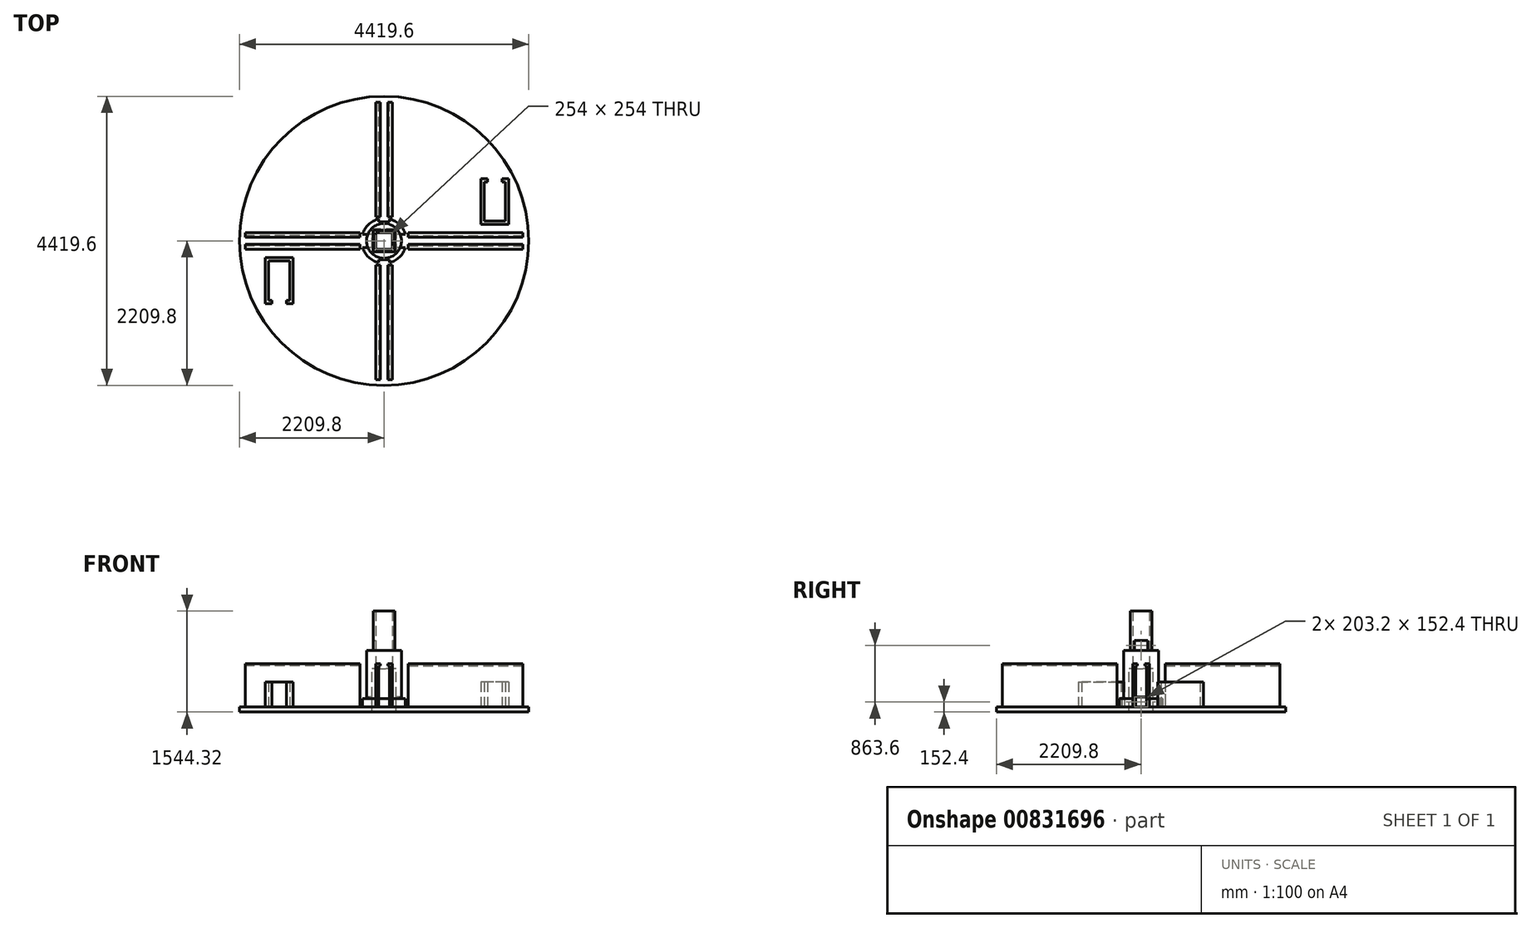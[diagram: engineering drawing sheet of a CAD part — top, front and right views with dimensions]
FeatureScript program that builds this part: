
annotation { "Feature Type Name" : "Feature", "Feature Type Description" : "" }
export const myFeature = defineFeature(function(context is Context, id is Id, definition is map)
    precondition{}
    {
        {
            var Q0;
            Q0=qCreatedBy(makeId("Top.planeOp"),FACE);
            var sketch = newSketch(context, id + "F0", { "sketchPlane" : qUnion([Q0])});
            skCircle(sketch, "E0", {"center": v(0, 0) * mm, "radius": 2209.8 * mm});
            skCircle(sketch, "E1", {"center": v(0, 0) * mm, "radius": 266.7 * mm});
            skLineSegment(sketch, "E2.bottom", {"start": v(-127, -127) * mm, "end": v(127, -127) * mm});
            skLineSegment(sketch, "E2.top", {"start": v(-127, 127) * mm, "end": v(127, 127) * mm});
            skLineSegment(sketch, "E2.left", {"start": v(-127, -127) * mm, "end": v(-127, 127) * mm});
            skLineSegment(sketch, "E2.right", {"start": v(127, -127) * mm, "end": v(127, 127) * mm});
            skLineSegment(sketch, "E3.bottom", {"start": v(-177.8, 177.8) * mm, "end": v(177.8, 177.8) * mm});
            skLineSegment(sketch, "E3.top", {"start": v(-177.8, -177.8) * mm, "end": v(177.8, -177.8) * mm});
            skLineSegment(sketch, "E3.left", {"start": v(-177.8, 177.8) * mm, "end": v(-177.8, -177.8) * mm});
            skLineSegment(sketch, "E3.right", {"start": v(177.8, 177.8) * mm, "end": v(177.8, -177.8) * mm});
            skLineSegment(sketch, "E4.bottom", {"start": v(182.88, 182.88) * mm, "end": v(-182.88, 182.88) * mm});
            skLineSegment(sketch, "E4.top", {"start": v(182.88, -182.88) * mm, "end": v(-182.88, -182.88) * mm});
            skLineSegment(sketch, "E4.left", {"start": v(182.88, 182.88) * mm, "end": v(182.88, -182.88) * mm});
            skLineSegment(sketch, "E4.right", {"start": v(-182.88, 182.88) * mm, "end": v(-182.88, -182.88) * mm});
            skPoint(sketch, "E5", {"position": v(0, 266.7) * mm});
            skPoint(sketch, "E6", {"position": v(266.7, 0) * mm});
            skPoint(sketch, "E7", {"position": v(0, -266.7) * mm});
            skLineSegment(sketch, "E8.bottom", {"start": v(-127, -2120.9) * mm, "end": v(127, -2120.9) * mm});
            skLineSegment(sketch, "E8.top", {"start": v(-127, -368.3) * mm, "end": v(127, -368.3) * mm});
            skLineSegment(sketch, "E8.left", {"start": v(-127, -2120.9) * mm, "end": v(-127, -368.3) * mm});
            skLineSegment(sketch, "E8.right", {"start": v(127, -2120.9) * mm, "end": v(127, -368.3) * mm});
            skLineSegment(sketch, "E9.bottom", {"start": v(368.3, -127) * mm, "end": v(2120.9, -127) * mm});
            skLineSegment(sketch, "E9.top", {"start": v(368.3, 127) * mm, "end": v(2120.9, 127) * mm});
            skLineSegment(sketch, "E9.left", {"start": v(368.3, -127) * mm, "end": v(368.3, 127) * mm});
            skLineSegment(sketch, "E9.right", {"start": v(2120.9, -127) * mm, "end": v(2120.9, 127) * mm});
            skLineSegment(sketch, "E10.bottom", {"start": v(-127, 368.3) * mm, "end": v(127, 368.3) * mm});
            skLineSegment(sketch, "E10.top", {"start": v(-127, 2120.9) * mm, "end": v(127, 2120.9) * mm});
            skLineSegment(sketch, "E10.left", {"start": v(-127, 368.3) * mm, "end": v(-127, 2120.9) * mm});
            skLineSegment(sketch, "E10.right", {"start": v(127, 368.3) * mm, "end": v(127, 2120.9) * mm});
            skCircle(sketch, "E11", {"center": v(0, 0) * mm, "radius": 368.3 * mm});
            skPoint(sketch, "E12", {"position": v(0, 368.3) * mm});
            skPoint(sketch, "E13", {"position": v(368.3, 0) * mm});
            skPoint(sketch, "E14", {"position": v(0, -368.3) * mm});
            skPoint(sketch, "E15", {"position": v(-266.7, 0) * mm});
            skPoint(sketch, "E15.positionSnap0", {"position": v(-177.8, 0) * mm});
            skPoint(sketch, "E16", {"position": v(-368.3, 0) * mm});
            skLineSegment(sketch, "E17.bottom", {"start": v(-2120.9, -127) * mm, "end": v(-368.3, -127) * mm});
            skLineSegment(sketch, "E17.top", {"start": v(-2120.9, 127) * mm, "end": v(-368.3, 127) * mm});
            skLineSegment(sketch, "E17.left", {"start": v(-2120.9, -127) * mm, "end": v(-2120.9, 127) * mm});
            skLineSegment(sketch, "E17.right", {"start": v(-368.3, -127) * mm, "end": v(-368.3, 127) * mm});
            skCircle(sketch, "E18", {"center": v(0, 0) * mm, "radius": 342.9 * mm});
            skLineSegment(sketch, "E19.bottom", {"start": v(1854.2, 304.8) * mm, "end": v(1529.08, 304.8) * mm});
            skLineSegment(sketch, "E19.top", {"start": v(1854.2, 901.7) * mm, "end": v(1529.08, 901.7) * mm});
            skLineSegment(sketch, "E19.left", {"start": v(1854.2, 304.8) * mm, "end": v(1854.2, 901.7) * mm});
            skLineSegment(sketch, "E19.right", {"start": v(1529.08, 304.8) * mm, "end": v(1529.08, 901.7) * mm});
            skLineSegment(sketch, "E20.bottom", {"start": v(1905, 254) * mm, "end": v(1478.28, 254) * mm});
            skLineSegment(sketch, "E20.top", {"start": v(1905, 952.5) * mm, "end": v(1478.28, 952.5) * mm});
            skLineSegment(sketch, "E20.left", {"start": v(1905, 254) * mm, "end": v(1905, 952.5) * mm});
            skLineSegment(sketch, "E20.right", {"start": v(1478.28, 254) * mm, "end": v(1478.28, 952.5) * mm});
            skLineSegment(sketch, "E21", {"start": v(1579.88, 901.7) * mm, "end": v(1579.88, 952.5) * mm});
            skLineSegment(sketch, "E22", {"start": v(1803.4, 901.7) * mm, "end": v(1803.4, 952.5) * mm});
            skLineSegment(sketch, "E23.bottom", {"start": v(-1765.3, -304.8) * mm, "end": v(-1440.18, -304.8) * mm});
            skLineSegment(sketch, "E23.top", {"start": v(-1765.3, -909.32) * mm, "end": v(-1440.18, -909.32) * mm});
            skLineSegment(sketch, "E23.left", {"start": v(-1765.3, -304.8) * mm, "end": v(-1765.3, -909.32) * mm});
            skLineSegment(sketch, "E23.right", {"start": v(-1440.18, -304.8) * mm, "end": v(-1440.18, -909.32) * mm});
            skPoint(sketch, "E23.middle", {"position": v(-1602.74, -607.06) * mm});
            skLineSegment(sketch, "E24.bottom", {"start": v(-1389.38, -960.12) * mm, "end": v(-1816.1, -960.12) * mm});
            skLineSegment(sketch, "E24.top", {"start": v(-1389.38, -254) * mm, "end": v(-1816.1, -254) * mm});
            skLineSegment(sketch, "E24.left", {"start": v(-1389.38, -960.12) * mm, "end": v(-1389.38, -254) * mm});
            skLineSegment(sketch, "E24.right", {"start": v(-1816.1, -960.12) * mm, "end": v(-1816.1, -254) * mm});
            skLineSegment(sketch, "E25", {"start": v(-1490.98, -909.32) * mm, "end": v(-1490.98, -960.12) * mm});
            skLineSegment(sketch, "E26", {"start": v(-1714.5, -960.12) * mm, "end": v(-1714.5, -909.32) * mm});
            skSolve(sketch);
        }
        {
            var Q0;
            Q0=makeQuery(id+"F0.imprint","IMPRINT",FACE,{"disambiguationData":[TD([[makeQuery(id+"F0.imprint","IMPRINT",EDGE,{"derivedFrom":sQuery(id+"F0.wireOp",EDGE,"E10.top")}),-1.0]])]});
            var Q1;
            Q1=makeQuery(id+"F0.imprint","IMPRINT",FACE,{"disambiguationData":[TD([[makeQuery(id+"F0.imprint","IMPRINT",EDGE,{"derivedFrom":sQuery(id+"F0.wireOp",EDGE,"E1")}),-1.0]])]});
            var Q2;
            Q2=makeQuery(id+"F0.imprint","IMPRINT",FACE,{"disambiguationData":[TD([[makeQuery(id+"F0.imprint","IMPRINT",EDGE,{"derivedFrom":sQuery(id+"F0.wireOp",EDGE,"E1")}),1.0]])]});
            var Q3;
            {var subQ4=sQuery(id+"F0.wireOp",EDGE,"E9.bottom");Q3=makeQuery(id+"F0.imprint","IMPRINT",FACE,{"disambiguationData":[TD([[makeQuery(id+"F0.imprint","IMPRINT",EDGE,{"derivedFrom":subQ4}),1.0]])]});}
            var Q4;
            {var subQ0=sQuery(id+"F0.wireOp",EDGE,"E17.bottom");Q4=makeQuery(id+"F0.imprint","IMPRINT",FACE,{"disambiguationData":[TD([[makeQuery(id+"F0.imprint","IMPRINT",EDGE,{"derivedFrom":subQ0}),1.0]])]});}
            var Q5;
            Q5=makeQuery(id+"F0.imprint","IMPRINT",FACE,{"disambiguationData":[TD([[makeQuery(id+"F0.imprint","IMPRINT",EDGE,{"derivedFrom":sQuery(id+"F0.wireOp",EDGE,"E8.bottom")}),1.0]])]});
            var Q6;
            Q6=makeQuery(id+"F0.imprint","IMPRINT",FACE,{"disambiguationData":[TD([[makeQuery(id+"F0.imprint","IMPRINT",EDGE,{"derivedFrom":sQuery(id+"F0.wireOp",EDGE,"E18")}),-1.0]])]});
            var Q7;
            Q7=makeQuery(id+"F0.imprint","IMPRINT",FACE,{"disambiguationData":[TD([[makeQuery(id+"F0.imprint","IMPRINT",EDGE,{"derivedFrom":sQuery(id+"F0.wireOp",EDGE,"E0")}),1.0]])]});
            var Q8;
            Q8=makeQuery(id+"F0.imprint","IMPRINT",FACE,{"disambiguationData":[TD([[makeQuery(id+"F0.imprint","IMPRINT",EDGE,{"derivedFrom":sQuery(id+"F0.wireOp",EDGE,"b8a19175-b3a9-4f45-8a98-ed4f9f6c6702.bottom")}),-1.0]])]});
            var Q9;
            Q9=makeQuery(id+"F0.imprint","IMPRINT",FACE,{"disambiguationData":[TD([[makeQuery(id+"F0.imprint","IMPRINT",EDGE,{"derivedFrom":sQuery(id+"F0.wireOp",EDGE,"7914a9b4-7248-453b-a2e4-3dba9f99fffc.bottom")}),1.0]])]});
            var Q10;
            {var subQ0=sQuery(id+"F0.wireOp",EDGE,"TmSJG6FK-Om5E-kqqE-cBKC-40XiXbPmcmxI");Q10=makeQuery(id+"F0.imprint","IMPRINT",FACE,{"disambiguationData":[TD([[makeQuery(id+"F0.imprint","IMPRINT",EDGE,{"derivedFrom":subQ0}),1.0]])]});}
            var Q11;
            Q11=makeQuery(id+"F0.imprint","IMPRINT",FACE,{"disambiguationData":[TD([[makeQuery(id+"F0.imprint","IMPRINT",EDGE,{"derivedFrom":sQuery(id+"F0.wireOp",EDGE,"wxg1OY8f-ebEG-U6Dd-82FZ-Xdf4qu9MraA2.bottom")}),1.0]])]});
            var Q12;
            {var subQ0=sQuery(id+"F0.wireOp",EDGE,"mW7lPLey-tL3F-X1Fa-1OeG-OaxEq5PTPofp");Q12=makeQuery(id+"F0.imprint","IMPRINT",FACE,{"disambiguationData":[TD([[makeQuery(id+"F0.imprint","IMPRINT",EDGE,{"derivedFrom":subQ0}),-1.0]])]});}
            var Q13;
            Q13=makeQuery(id+"F0.imprint","IMPRINT",FACE,{"disambiguationData":[TD([[makeQuery(id+"F0.imprint","IMPRINT",EDGE,{"derivedFrom":sQuery(id+"F0.wireOp",EDGE,"IBWuTJHf-9YuP-0ksT-Em6A-mQtnpUZ14kUv.top")}),1.0]])]});
            var Q14;
            Q14=makeQuery(id+"F0.imprint","IMPRINT",FACE,{"disambiguationData":[TD([[makeQuery(id+"F0.imprint","IMPRINT",EDGE,{"derivedFrom":sQuery(id+"F0.wireOp",EDGE,"E19.bottom")}),-1.0]])]});
            var Q15;
            Q15=makeQuery(id+"F0.imprint","IMPRINT",FACE,{"disambiguationData":[TD([[makeQuery(id+"F0.imprint","IMPRINT",EDGE,{"derivedFrom":sQuery(id+"F0.wireOp",EDGE,"E19.bottom")}),1.0]])]});
            var Q16;
            {var subQ0=sQuery(id+"F0.wireOp",EDGE,"E21");Q16=makeQuery(id+"F0.imprint","IMPRINT",FACE,{"disambiguationData":[TD([[makeQuery(id+"F0.imprint","IMPRINT",EDGE,{"derivedFrom":subQ0}),-1.0]])]});}
            var Q17;
            Q17=makeQuery(id+"F0.imprint","IMPRINT",FACE,{"disambiguationData":[TD([[makeQuery(id+"F0.imprint","IMPRINT",EDGE,{"derivedFrom":sQuery(id+"F0.wireOp",EDGE,"E23.bottom")}),-1.0]])]});
            var Q18;
            Q18=makeQuery(id+"F0.imprint","IMPRINT",FACE,{"disambiguationData":[TD([[makeQuery(id+"F0.imprint","IMPRINT",EDGE,{"derivedFrom":sQuery(id+"F0.wireOp",EDGE,"E23.bottom")}),1.0]])]});
            var Q19;
            {var subQ0=sQuery(id+"F0.wireOp",EDGE,"E25");Q19=makeQuery(id+"F0.imprint","IMPRINT",FACE,{"disambiguationData":[TD([[makeQuery(id+"F0.imprint","IMPRINT",EDGE,{"derivedFrom":subQ0}),-1.0]])]});}
            extrude(context, id + "F1", {"entities" : qUnion([Q0, Q1, Q2, Q3, Q4, Q5, Q6, Q7, Q8, Q9, Q10, Q11, Q12, Q13, Q14, Q15, Q16, Q17, Q18, Q19]), "oppositeDirection" : true, "depth" : 76.2 * mm, "offsetDistance" : 25.4 * mm});
        }
        {
            var Q0;
            Q0=makeQuery(id+"F0.imprint","IMPRINT",FACE,{"disambiguationData":[TD([[makeQuery(id+"F0.imprint","IMPRINT",EDGE,{"derivedFrom":sQuery(id+"F0.wireOp",EDGE,"E1")}),1.0]])]});
            var Q1;
            Q1=makeQuery(id+"F0.imprint","IMPRINT",FACE,{"disambiguationData":[TD([[makeQuery(id+"F0.imprint","IMPRINT",EDGE,{"derivedFrom":sQuery(id+"F0.wireOp",EDGE,"E3.bottom")}),1.0]])]});
            var Q2;
            Q2=makeQuery(id+"F0.imprint","IMPRINT",FACE,{"disambiguationData":[TD([[makeQuery(id+"F0.imprint","IMPRINT",EDGE,{"derivedFrom":sQuery(id+"F0.wireOp",EDGE,"E2.bottom")}),-1.0]])]});
            extrude(context, id + "F2", {"entities" : qUnion([Q0, Q1, Q2]), "operationType" : NewBodyOperationType.ADD, "depth" : 863.6 * mm, "offsetDistance" : 25.4 * mm});
        }
        {
            var Q0;
            Q0=makeQuery(id+"F0.imprint","IMPRINT",FACE,{"disambiguationData":[TD([[makeQuery(id+"F0.imprint","IMPRINT",EDGE,{"derivedFrom":sQuery(id+"F0.wireOp",EDGE,"E2.bottom")}),-1.0]])]});
            var Q1;
            Q1=makeQuery(id+"F0.imprint","IMPRINT",FACE,{"disambiguationData":[TD([[makeQuery(id+"F0.imprint","IMPRINT",EDGE,{"derivedFrom":sQuery(id+"F0.wireOp",EDGE,"E2.bottom")}),1.0]])]});
            var Q2;
            Q2=makeQuery(id+"F0.imprint","IMPRINT",FACE,{"disambiguationData":[TD([[makeQuery(id+"F0.imprint","IMPRINT",EDGE,{"derivedFrom":sQuery(id+"F0.wireOp",EDGE,"E3.bottom")}),1.0]])]});
            extrude(context, id + "F3", {"entities" : qUnion([Q0, Q1, Q2]), "operationType" : NewBodyOperationType.REMOVE, "depth" : 584.2 * mm, "offsetDistance" : 25.4 * mm});
        }
        {
            var Q0;
            Q0=makeQuery(id+"F2.opExtrude","CAP_FACE",FACE,{"disambiguationData":[OSD([sQuery(id+"F0.wireOp",EDGE,"E1")])],"isStart":false});
            var sketch = newSketch(context, id + "F4", { "sketchPlane" : qUnion([Q0])});
            skLineSegment(sketch, "E27.bottom", {"start": v(-127, 127) * mm, "end": v(127, 127) * mm});
            skLineSegment(sketch, "E27.top", {"start": v(-127, -127) * mm, "end": v(127, -127) * mm});
            skLineSegment(sketch, "E27.left", {"start": v(-127, 127) * mm, "end": v(-127, -127) * mm});
            skLineSegment(sketch, "E27.right", {"start": v(127, 127) * mm, "end": v(127, -127) * mm});
            skPoint(sketch, "E27.middle", {"position": v(0, 0) * mm});
            skLineSegment(sketch, "E28.bottom", {"start": v(-165.1, 165.1) * mm, "end": v(165.1, 165.1) * mm});
            skLineSegment(sketch, "E28.top", {"start": v(-165.1, -165.1) * mm, "end": v(165.1, -165.1) * mm});
            skLineSegment(sketch, "E28.left", {"start": v(-165.1, 165.1) * mm, "end": v(-165.1, -165.1) * mm});
            skLineSegment(sketch, "E28.right", {"start": v(165.1, 165.1) * mm, "end": v(165.1, -165.1) * mm});
            skSolve(sketch);
        }
        {
            var Q0;
            Q0=makeQuery(id+"F4.imprint","IMPRINT",FACE,{"disambiguationData":[TD([[makeQuery(id+"F4.imprint","IMPRINT",EDGE,{"derivedFrom":sQuery(id+"F4.wireOp",EDGE,"E27.bottom")}),1.0]])]});
            extrude(context, id + "F5", {"entities" : qUnion([Q0]), "operationType" : NewBodyOperationType.ADD, "depth" : 604.52 * mm, "offsetDistance" : 25.4 * mm});
        }
        {
            var Q0;
            Q0=makeQuery(id+"F0.imprint","IMPRINT",FACE,{"disambiguationData":[TD([[makeQuery(id+"F0.imprint","IMPRINT",EDGE,{"derivedFrom":sQuery(id+"F0.wireOp",EDGE,"E1")}),-1.0]])]});
            extrude(context, id + "F6", {"entities" : qUnion([Q0]), "operationType" : NewBodyOperationType.ADD, "depth" : 127 * mm, "offsetDistance" : 25.4 * mm});
        }
        {
            var Q0;
            Q0=qCreatedBy(makeId("Right.planeOp"),FACE);
            var sketch = newSketch(context, id + "F7", { "sketchPlane" : qUnion([Q0])});
            skLineSegment(sketch, "E29.bottom", {"start": v(-101.6, 0) * mm, "end": v(101.6, 0) * mm});
            skLineSegment(sketch, "E29.top", {"start": v(-101.6, 152.4) * mm, "end": v(101.6, 152.4) * mm});
            skLineSegment(sketch, "E29.left", {"start": v(-101.6, 0) * mm, "end": v(-101.6, 152.4) * mm});
            skLineSegment(sketch, "E29.right", {"start": v(101.6, 0) * mm, "end": v(101.6, 152.4) * mm});
            skSolve(sketch);
        }
        {
            var Q0;
            Q0 = qSketchRegion(id + "F7", true);
            extrude(context, id + "F8", {"entities" : qUnion([Q0]), "operationType" : NewBodyOperationType.REMOVE, "endBound" : BoundingType.SYMMETRIC, "depth" : 701.04 * mm, "offsetDistance" : 25.4 * mm});
        }
        {
            var Q0;
            Q0=makeQuery(id+"F0.imprint","IMPRINT",FACE,{"disambiguationData":[TD([[makeQuery(id+"F0.imprint","IMPRINT",EDGE,{"derivedFrom":sQuery(id+"F0.wireOp",EDGE,"E8.bottom")}),1.0]])]});
            var Q1;
            {var subQ1=sQuery(id+"F0.wireOp",EDGE,"E17.bottom");Q1=makeQuery(id+"F0.imprint","IMPRINT",FACE,{"disambiguationData":[TD([[makeQuery(id+"F0.imprint","IMPRINT",EDGE,{"derivedFrom":subQ1}),1.0]])]});}
            var Q2;
            Q2=makeQuery(id+"F0.imprint","IMPRINT",FACE,{"disambiguationData":[TD([[makeQuery(id+"F0.imprint","IMPRINT",EDGE,{"derivedFrom":sQuery(id+"F0.wireOp",EDGE,"E10.top")}),-1.0]])]});
            var Q3;
            {var subQ1=sQuery(id+"F0.wireOp",EDGE,"E9.bottom");Q3=makeQuery(id+"F0.imprint","IMPRINT",FACE,{"disambiguationData":[TD([[makeQuery(id+"F0.imprint","IMPRINT",EDGE,{"derivedFrom":subQ1}),1.0]])]});}
            extrude(context, id + "F9", {"entities" : qUnion([Q0, Q1, Q2, Q3]), "operationType" : NewBodyOperationType.ADD, "depth" : 660.4 * mm, "offsetDistance" : 25.4 * mm});
        }
        {
            var Q0;
            Q0=makeQuery(id+"F9.opExtrude","SWEPT_FACE",FACE,{"disambiguationData":[OSD([sQuery(id+"F0.wireOp",EDGE,"E8.bottom")])]});
            var sketch = newSketch(context, id + "F10", { "sketchPlane" : qUnion([Q0])});
            skLineSegment(sketch, "E30.bottom", {"start": v(-81.28, 629.92) * mm, "end": v(81.28, 629.92) * mm});
            skLineSegment(sketch, "E30.top", {"start": v(-81.28, 0) * mm, "end": v(81.28, 0) * mm});
            skLineSegment(sketch, "E30.left", {"start": v(-81.28, 629.92) * mm, "end": v(-81.28, 0) * mm});
            skLineSegment(sketch, "E30.right", {"start": v(81.28, 629.92) * mm, "end": v(81.28, 0) * mm});
            skLineSegment(sketch, "E31.bottom", {"start": v(-55.88, 629.92) * mm, "end": v(55.88, 629.92) * mm});
            skLineSegment(sketch, "E31.top", {"start": v(-55.88, 660.4) * mm, "end": v(55.88, 660.4) * mm});
            skLineSegment(sketch, "E31.left", {"start": v(-55.88, 629.92) * mm, "end": v(-55.88, 660.4) * mm});
            skLineSegment(sketch, "E31.right", {"start": v(55.88, 629.92) * mm, "end": v(55.88, 660.4) * mm});
            skSolve(sketch);
        }
        {
            var Q0;
            Q0=makeQuery(id+"F10.imprint","IMPRINT",FACE,{"disambiguationData":[TD([[makeQuery(id+"F10.imprint","IMPRINT",EDGE,{"derivedFrom":sQuery(id+"F10.wireOp",EDGE,"E30.top")}),1.0]])]});
            var Q1;
            {var subQ0=sQuery(id+"F10.wireOp",EDGE,"E31.top");Q1=makeQuery(id+"F10.imprint","IMPRINT",FACE,{"disambiguationData":[TD([[makeQuery(id+"F10.imprint","IMPRINT",EDGE,{"derivedFrom":subQ0}),-1.0]])]});}
            var Q2;
            {var subQ0=sQuery(id+"F10.wireOp",EDGE,"E31.bottom");Q2=makeQuery(id+"F10.imprint","IMPRINT",FACE,{"disambiguationData":[TD([[makeQuery(id+"F10.imprint","IMPRINT",EDGE,{"derivedFrom":subQ0}),1.0]])]});}
            extrude(context, id + "F11", {"entities" : qUnion([Q0, Q1, Q2]), "operationType" : NewBodyOperationType.REMOVE, "oppositeDirection" : true, "depth" : 1832.36 * mm, "offsetDistance" : 25.4 * mm});
        }
        {
            var Q0;
            Q0=makeQuery(id+"F9.opExtrude","SWEPT_FACE",FACE,{"disambiguationData":[OSD([sQuery(id+"F0.wireOp",EDGE,"E17.left")])]});
            var sketch = newSketch(context, id + "F12", { "sketchPlane" : qUnion([Q0])});
            skLineSegment(sketch, "E32.bottom", {"start": v(-81.28, 629.92) * mm, "end": v(81.28, 629.92) * mm});
            skLineSegment(sketch, "E32.top", {"start": v(-81.28, 0) * mm, "end": v(81.28, 0) * mm});
            skLineSegment(sketch, "E32.left", {"start": v(-81.28, 629.92) * mm, "end": v(-81.28, 0) * mm});
            skLineSegment(sketch, "E32.right", {"start": v(81.28, 629.92) * mm, "end": v(81.28, 0) * mm});
            skLineSegment(sketch, "E33.bottom", {"start": v(-55.88, 629.92) * mm, "end": v(55.88, 629.92) * mm});
            skLineSegment(sketch, "E33.top", {"start": v(-55.88, 661.55) * mm, "end": v(55.88, 661.55) * mm});
            skLineSegment(sketch, "E33.left", {"start": v(-55.88, 629.92) * mm, "end": v(-55.88, 661.55) * mm});
            skLineSegment(sketch, "E33.right", {"start": v(55.88, 629.92) * mm, "end": v(55.88, 661.55) * mm});
            skSolve(sketch);
        }
        {
            var Q0;
            Q0 = qSketchRegion(id + "F12", true);
            extrude(context, id + "F13", {"entities" : qUnion([Q0]), "operationType" : NewBodyOperationType.REMOVE, "oppositeDirection" : true, "depth" : 1793.24 * mm, "offsetDistance" : 25.4 * mm});
        }
        {
            var Q0;
            Q0=makeQuery(id+"F9.opExtrude","SWEPT_FACE",FACE,{"disambiguationData":[OSD([sQuery(id+"F0.wireOp",EDGE,"E10.top")])]});
            var sketch = newSketch(context, id + "F14", { "sketchPlane" : qUnion([Q0])});
            skLineSegment(sketch, "E34.bottom", {"start": v(-81.28, 629.92) * mm, "end": v(81.28, 629.92) * mm});
            skLineSegment(sketch, "E34.top", {"start": v(-81.28, 0) * mm, "end": v(81.28, 0) * mm});
            skLineSegment(sketch, "E34.left", {"start": v(-81.28, 629.92) * mm, "end": v(-81.28, 0) * mm});
            skLineSegment(sketch, "E34.right", {"start": v(81.28, 629.92) * mm, "end": v(81.28, 0) * mm});
            skLineSegment(sketch, "E35.bottom", {"start": v(-55.88, 629.92) * mm, "end": v(55.88, 629.92) * mm});
            skLineSegment(sketch, "E35.top", {"start": v(-55.88, 661.55) * mm, "end": v(55.88, 661.55) * mm});
            skLineSegment(sketch, "E35.left", {"start": v(-55.88, 629.92) * mm, "end": v(-55.88, 661.55) * mm});
            skLineSegment(sketch, "E35.right", {"start": v(55.88, 629.92) * mm, "end": v(55.88, 661.55) * mm});
            skSolve(sketch);
        }
        {
            var Q0;
            Q0 = qSketchRegion(id + "F14", true);
            extrude(context, id + "F15", {"entities" : qUnion([Q0]), "operationType" : NewBodyOperationType.REMOVE, "oppositeDirection" : true, "depth" : 1833.88 * mm, "offsetDistance" : 25.4 * mm});
        }
        {
            var Q0;
            Q0=makeQuery(id+"F9.opExtrude","SWEPT_FACE",FACE,{"disambiguationData":[OSD([sQuery(id+"F0.wireOp",EDGE,"E9.right")])]});
            var sketch = newSketch(context, id + "F16", { "sketchPlane" : qUnion([Q0])});
            skLineSegment(sketch, "E36.bottom", {"start": v(-81.28, 629.92) * mm, "end": v(81.28, 629.92) * mm});
            skLineSegment(sketch, "E36.top", {"start": v(-81.28, 0) * mm, "end": v(81.28, 0) * mm});
            skLineSegment(sketch, "E36.left", {"start": v(-81.28, 629.92) * mm, "end": v(-81.28, 0) * mm});
            skLineSegment(sketch, "E36.right", {"start": v(81.28, 629.92) * mm, "end": v(81.28, 0) * mm});
            skLineSegment(sketch, "E37.bottom", {"start": v(-55.88, 629.92) * mm, "end": v(55.88, 629.92) * mm});
            skLineSegment(sketch, "E37.top", {"start": v(-55.88, 661.55) * mm, "end": v(55.88, 661.55) * mm});
            skLineSegment(sketch, "E37.left", {"start": v(-55.88, 629.92) * mm, "end": v(-55.88, 661.55) * mm});
            skLineSegment(sketch, "E37.right", {"start": v(55.88, 629.92) * mm, "end": v(55.88, 661.55) * mm});
            skSolve(sketch);
        }
        {
            var Q0;
            Q0 = qSketchRegion(id + "F16", true);
            extrude(context, id + "F17", {"entities" : qUnion([Q0]), "operationType" : NewBodyOperationType.REMOVE, "oppositeDirection" : true, "depth" : 1811.02 * mm, "offsetDistance" : 25.4 * mm});
        }
        {
            var Q0;
            Q0=makeQuery(id+"F0.imprint","IMPRINT",FACE,{"disambiguationData":[TD([[makeQuery(id+"F0.imprint","IMPRINT",EDGE,{"derivedFrom":sQuery(id+"F0.wireOp",EDGE,"E23.bottom")}),1.0]])]});
            var Q1;
            Q1=makeQuery(id+"F0.imprint","IMPRINT",FACE,{"disambiguationData":[TD([[makeQuery(id+"F0.imprint","IMPRINT",EDGE,{"derivedFrom":sQuery(id+"F0.wireOp",EDGE,"E19.bottom")}),1.0]])]});
            extrude(context, id + "F18", {"entities" : qUnion([Q0, Q1]), "operationType" : NewBodyOperationType.ADD, "depth" : 381 * mm, "offsetDistance" : 25.4 * mm});
        }
        {
            var Q0;
            Q0=makeQuery(id+"F5.opExtrude","SWEPT_FACE",FACE,{"disambiguationData":[OSD([sQuery(id+"F4.wireOp",EDGE,"E28.right")])]});
            var sketch = newSketch(context, id + "F19", { "sketchPlane" : qUnion([Q0])});
            skLineSegment(sketch, "E38.bottom", {"start": v(-101.6, 863.6) * mm, "end": v(101.6, 863.6) * mm});
            skLineSegment(sketch, "E38.top", {"start": v(-101.6, 1016) * mm, "end": v(101.6, 1016) * mm});
            skLineSegment(sketch, "E38.left", {"start": v(-101.6, 863.6) * mm, "end": v(-101.6, 1016) * mm});
            skLineSegment(sketch, "E38.right", {"start": v(101.6, 863.6) * mm, "end": v(101.6, 1016) * mm});
            skPoint(sketch, "E38.middle", {"position": v(0, 939.8) * mm});
            skSolve(sketch);
        }
        {
            var Q0;
            Q0=makeQuery(id+"F19.imprint","IMPRINT",FACE,{"disambiguationData":[TD([[makeQuery(id+"F19.imprint","IMPRINT",EDGE,{"derivedFrom":sQuery(id+"F19.wireOp",EDGE,"E38.bottom")}),-1.0]])]});
            extrude(context, id + "F20", {"entities" : qUnion([Q0]), "operationType" : NewBodyOperationType.REMOVE, "oppositeDirection" : true, "depth" : 347.47 * mm, "offsetDistance" : 25.4 * mm});
        }
    });
